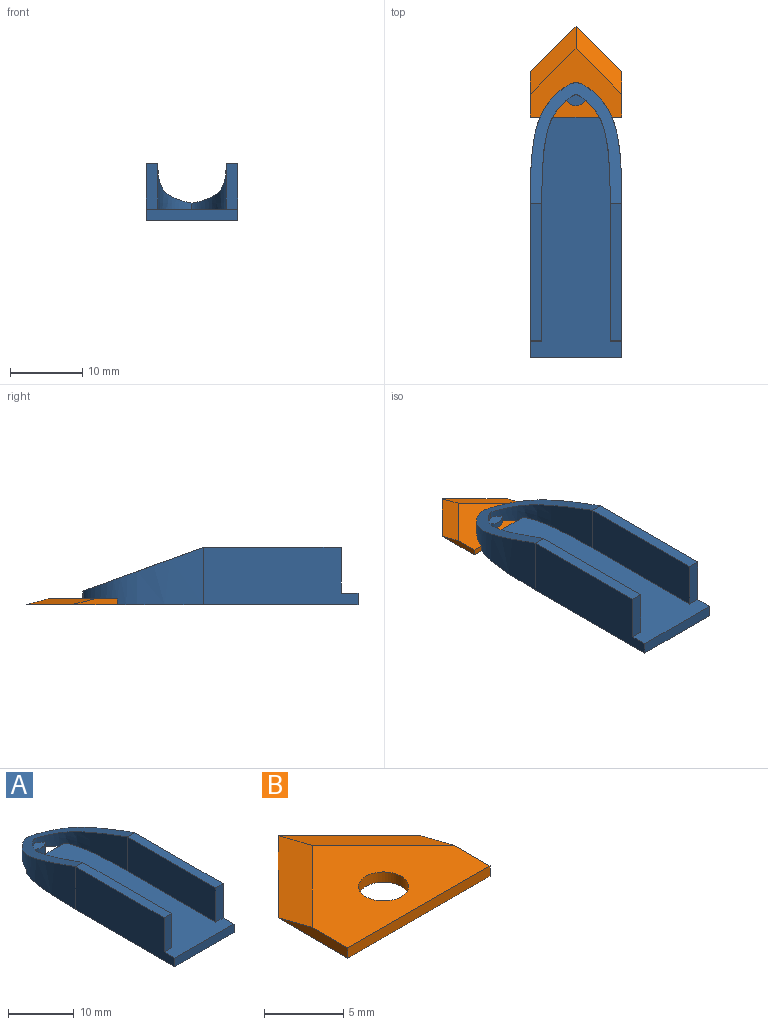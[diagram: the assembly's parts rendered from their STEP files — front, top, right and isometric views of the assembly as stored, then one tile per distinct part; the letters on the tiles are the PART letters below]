
ASSEMBLY  parts=2 mates=1
PART A: 25 faces, bbox 12.7x38.1x7.9 mm
  f0: plane 9.96x1.59mm, normal (0,1,0), area 13mm2, adj f1,f3,f9,f10,f15,f16,f22,f23
  f1: plane 33.66x12.7mm, normal (0,0,-1), area 415.4mm2, adj f0,f2,f6,f7,f10,f16,f24
  f2: plane 21.39x7.94mm, normal (-1,0,0), area 154.9mm2, adj f1,f3,f7,f10,f12,f14
  f3: plane 33.36x12.7mm, normal (0,0,1), area 316.4mm2, adj f0,f2,f6,f7,f9,f13,f14,f15
  f4: plane 2.66x1.58mm, normal (0,0,1), area 2.6mm2, adj f9,f15,f20
  f5: plane 0.74x0.19mm, normal (0,0,1), area 0mm2, adj f16,f20
  f6: plane 21.39x7.94mm, normal (1,0,0), area 154.9mm2, adj f1,f3,f7,f16,f17,f19,f24
  f7: plane 12.7x1.59mm, normal (0,-1,0), area 20.2mm2, adj f1,f2,f3,f6
  f8: plane 0.74x0.19mm, normal (0,0,1), area 0mm2, adj f10,f20
  f9: extruded ~15.11x7.14mm, area 59.1mm2, adj f0,f3,f4,f11,f13,f15,f20,f22
  f10: extruded ~16.71x7.94mm, area 81.6mm2, adj f0,f1,f2,f8,f11,f16,f20,f22
  f11: plane 16.71x12.7mm, normal (0,0.34,0.94), area 60.8mm2, adj f9,f10,f12,f15,f16,f17
  f12: plane 19.05x1.59mm, normal (0,0,1), area 30.2mm2, adj f2,f11,f13,f14
  f13: plane 19.05x6.35mm, normal (1,0,0), area 121mm2, adj f3,f9,f12,f14
  f14: plane 6.35x1.59mm, normal (0,-1,0), area 10.1mm2, adj f2,f3,f12,f13
  f15: extruded ~15.11x7.14mm, area 59.1mm2, adj f0,f3,f4,f9,f11,f18,f20,f23
  f16: extruded ~16.71x7.94mm, area 63.7mm2, adj f0,f1,f5,f6,f10,f11,f20,f23
  f17: plane 19.05x1.59mm, normal (0,0,1), area 30.2mm2, adj f6,f11,f18,f19
  f18: plane 19.05x6.35mm, normal (-1,0,0), area 121mm2, adj f3,f15,f17,f19
  f19: plane 6.35x1.59mm, normal (0,-1,0), area 10.1mm2, adj f3,f6,f17,f18
  f20: cylinder r=1.59mm len=3.18mm, axis (0,0,-1), area 11.6mm2, adj f4,f5,f8,f9,f10,f15,f16,f21
  f21: plane 3.18x3.18mm, normal (0,0,-1), area 7.9mm2, adj f20
  f22: plane 4.7x4.37mm, normal (0,0,-1), area 6.7mm2, adj f0,f9,f10,f20
  f23: plane 4.7x4.37mm, normal (0,0,-1), area 6.7mm2, adj f0,f15,f16,f20
  f24: extruded ~11.19x1.59mm, area 17.9mm2, adj f1,f6,f16
PART B: 8 faces, bbox 12.7x12.6x0.8 mm
  f0: plane 6.26x0.79mm, normal (1,0,0), area 3.7mm2, adj f1,f2,f5,f6
  f1: plane 9.43x6.35mm, normal (0.24,0.24,0.94), area 20.8mm2, adj f0,f2,f4,f6
  f2: plane 12.7x12.61mm, normal (0,0,-1), area 111.9mm2, adj f0,f1,f3,f4,f5,f7
  f3: plane 6.26x0.79mm, normal (-1,0,0), area 3.7mm2, adj f2,f4,f5,f6
  f4: plane 9.43x6.35mm, normal (-0.24,0.24,0.94), area 20.8mm2, adj f1,f2,f3,f6
  f5: plane 12.7x0.79mm, normal (0,-1,0), area 10.1mm2, adj f0,f2,f3,f6
  f6: plane 12.7x9.53mm, normal (0,0,1), area 72.7mm2, adj f0,f1,f3,f4,f5,f7
  f7: cylinder r=1.59mm len=3.18mm, axis (0,0,1), area 7.9mm2, adj f2,f6
PLACE A t=(-11.47,-11.46,-3.14)mm
PLACE B t=(-11.47,12.35,-3.14)mm
MATE fastened B.f7 <-> A.f20  axis (0,0,-1) through (-11.47,6,-3.14)mm
